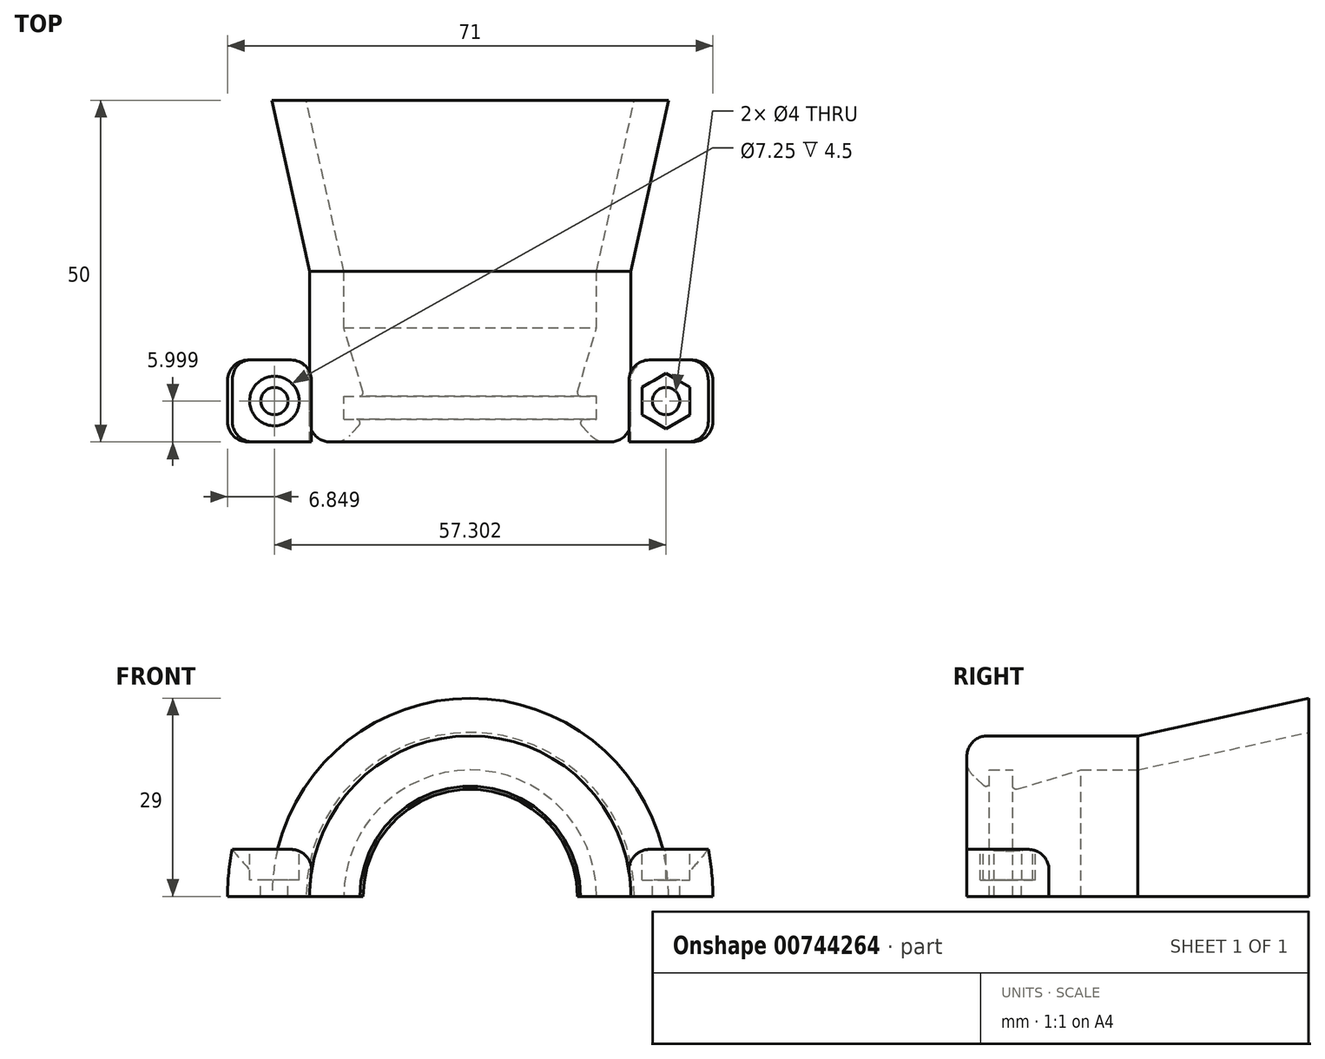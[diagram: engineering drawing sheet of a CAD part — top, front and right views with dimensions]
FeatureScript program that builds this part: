
annotation { "Feature Type Name" : "Feature", "Feature Type Description" : "" }
export const myFeature = defineFeature(function(context is Context, id is Id, definition is map)
    precondition{}
    {
        {
            var Q0;
            Q0=qCreatedBy(makeId("Top.planeOp"),FACE);
            var sketch = newSketch(context, id + "F0", { "sketchPlane" : qUnion([Q0])});
            skLineSegment(sketch, "E0", {"start": v(0, 30.3) * mm, "end": v(0, -19.7) * mm, "construction": true});
            skLineSegment(sketch, "E1", {"start": v(0, 30.3) * mm, "end": v(0, -14.7) * mm, "construction": true});
            skLineSegment(sketch, "E2", {"start": v(0, -19.7) * mm, "end": v(18.5, -19.7) * mm, "construction": true});
            skLineSegment(sketch, "E3.bottom", {"start": v(18.5, -19.7) * mm, "end": v(23.5, -19.7) * mm});
            skLineSegment(sketch, "E3.left", {"start": v(18.5, -16.4) * mm, "end": v(18.5, -13) * mm});
            skLineSegment(sketch, "E3.right", {"start": v(23.5, -19.7) * mm, "end": v(23.5, 5.3) * mm});
            skLineSegment(sketch, "E4", {"start": v(0, -14.7) * mm, "end": v(23.5, -14.7) * mm, "construction": true});
            skLineSegment(sketch, "E5", {"start": v(18.5, -14.7) * mm, "end": v(18.5, -14.7) * mm});
            skLineSegment(sketch, "E6", {"start": v(18.5, -14.7) * mm, "end": v(15.5, -14.7) * mm, "construction": true});
            skLineSegment(sketch, "E7", {"start": v(18.5, -14.7) * mm, "end": v(18.5, -16.4) * mm, "construction": true});
            skLineSegment(sketch, "E8", {"start": v(18.5, -14.7) * mm, "end": v(18.5, -13) * mm, "construction": true});
            skLineSegment(sketch, "E9", {"start": v(18.5, -16.4) * mm, "end": v(15.5, -16.4) * mm});
            skLineSegment(sketch, "E10", {"start": v(15.5, -16.4) * mm, "end": v(18.5, -19.7) * mm});
            skLineSegment(sketch, "E11", {"start": v(18.5, -13) * mm, "end": v(15.5, -13) * mm});
            skLineSegment(sketch, "E12", {"start": v(15.5, -13) * mm, "end": v(18.5, -3) * mm});
            skLineSegment(sketch, "E13.trimOffspring", {"start": v(18.5, -3) * mm, "end": v(18.5, 5.3) * mm});
            skLineSegment(sketch, "E14.bottom", {"start": v(23.5, -19.7) * mm, "end": v(30.5, -19.7) * mm});
            skLineSegment(sketch, "E14.top", {"start": v(23.5, -12.7) * mm, "end": v(30.5, -12.7) * mm});
            skLineSegment(sketch, "E14.left", {"start": v(23.5, -19.7) * mm, "end": v(23.5, -12.7) * mm});
            skLineSegment(sketch, "E14.right", {"start": v(30.5, -19.7) * mm, "end": v(30.5, -12.7) * mm});
            skLineSegment(sketch, "E15", {"start": v(0, 30.3) * mm, "end": v(18.5, 30.3) * mm, "construction": true});
            skLineSegment(sketch, "E16", {"start": v(18.5, 5.3) * mm, "end": v(24, 30.3) * mm});
            skLineSegment(sketch, "E17", {"start": v(23.5, 5.3) * mm, "end": v(29, 30.3) * mm});
            skLineSegment(sketch, "E18", {"start": v(24, 30.3) * mm, "end": v(29, 30.3) * mm});
            skPoint(sketch, "E3.top.end.orphan", {"position": v(23.5, 30.3) * mm});
            skLineSegment(sketch, "E19.bottom", {"start": v(23.5, -19.7) * mm, "end": v(35.5, -19.7) * mm});
            skLineSegment(sketch, "E19.top", {"start": v(23.5, -7.7) * mm, "end": v(35.5, -7.7) * mm});
            skLineSegment(sketch, "E19.left", {"start": v(23.5, -19.7) * mm, "end": v(23.5, -7.7) * mm});
            skLineSegment(sketch, "E19.right", {"start": v(35.5, -19.7) * mm, "end": v(35.5, -7.7) * mm});
            skSolve(sketch);
        }
        {
            var Q0;
            {var subQ3=sQuery(id+"F0.wireOp",EDGE,"E3.bottom");Q0=makeQuery(id+"F0.imprint","IMPRINT",FACE,{"disambiguationData":[TD([[makeQuery(id+"F0.imprint","IMPRINT",EDGE,{"derivedFrom":subQ3}),1.0]])]});}
            var Q1;
            Q1=sQuery(id+"F0.wireOp",EDGE,"E0");
            revolve(context, id + "F1", {"surfaceOperationType" : NewSurfaceOperationType.NEW, "entities" : qUnion([Q0]), "axis" : qUnion([Q1]), "revolveType" : RevolveType.ONE_DIRECTION, "angle" : 180 * degree});
        }
        {
            var Q0;
            Q0=makeQuery(id+"F1.opRevolve","SWEPT_EDGE",EDGE,{"disambiguationData":[OSD([sQuery(id+"F0.wireOp",EDGE,"E9"),sQuery(id+"F0.wireOp",EDGE,"E10")])]});
            var Q1;
            Q1=makeQuery(id+"F1.opRevolve","SWEPT_EDGE",EDGE,{"disambiguationData":[OSD([sQuery(id+"F0.wireOp",EDGE,"E11"),sQuery(id+"F0.wireOp",EDGE,"E12")])]});
            fillet(context, id + "F2", {"entities" : qUnion([Q0, Q1]), "radius" : 0.5 * mm, "tangentPropagation" : true, "allowEdgeOverflow" : false});
        }
        {
            var Q0;
            {var subQ0=sQuery(id+"F0.wireOp",EDGE,"E14.top");Q0=makeQuery(id+"F0.imprint","IMPRINT",FACE,{"disambiguationData":[TD([[makeQuery(id+"F0.imprint","IMPRINT",EDGE,{"derivedFrom":subQ0}),1.0]])]});}
            var Q1;
            {var subQ0=sQuery(id+"F0.wireOp",EDGE,"E14.bottom");Q1=makeQuery(id+"F0.imprint","IMPRINT",FACE,{"disambiguationData":[TD([[makeQuery(id+"F0.imprint","IMPRINT",EDGE,{"derivedFrom":subQ0}),1.0]])]});}
            var Q2;
            Q2=sQuery(id+"F0.wireOp",EDGE,"E0");
            revolve(context, id + "F3", {"surfaceOperationType" : NewSurfaceOperationType.NEW, "entities" : qUnion([Q0, Q1]), "axis" : qUnion([Q2]), "revolveType" : RevolveType.ONE_DIRECTION, "angle" : 17 * degree});
        }
        {
            var Q0;
            Q0=makeQuery(id+"F3.opRevolve","SWEPT_BODY",BODY,{"disambiguationData":[OSD([sQuery(id+"F0.wireOp",EDGE,"E3.right"),sQuery(id+"F0.wireOp",EDGE,"E14.bottom"),sQuery(id+"F0.wireOp",EDGE,"E19.bottom"),sQuery(id+"F0.wireOp",EDGE,"E19.top"),sQuery(id+"F0.wireOp",EDGE,"E19.right")])]});
            var Q1;
            Q1=sQuery(id+"F0.wireOp",EDGE,"E0");
            circularPattern(context, id + "F4", {"entities" : qUnion([Q0]), "axis" : qUnion([Q1]), "angle" : 163 * degree, "instanceCount" : 2, "equalSpace" : true});
        }
        {
            var Q0;
            Q0=makeQuery(id+"F3.opRevolve","SWEPT_FACE",FACE,{"disambiguationData":[OSD([sQuery(id+"F0.wireOp",EDGE,"E14.bottom"),sQuery(id+"F0.wireOp",EDGE,"E19.bottom")])]});
            var sketch = newSketch(context, id + "F5", { "sketchPlane" : qUnion([Q0])});
            skLineSegment(sketch, "E20.bottom", {"start": v(22.47, 6.87) * mm, "end": v(38.75, 6.87) * mm});
            skLineSegment(sketch, "E20.top", {"start": v(22.47, 10.38) * mm, "end": v(38.75, 10.38) * mm});
            skLineSegment(sketch, "E20.left", {"start": v(22.47, 6.87) * mm, "end": v(22.47, 10.38) * mm});
            skLineSegment(sketch, "E20.right", {"start": v(38.75, 6.87) * mm, "end": v(38.75, 10.38) * mm});
            skSolve(sketch);
        }
        {
            var Q0;
            {var subQ1=sQuery(id+"F0.wireOp",EDGE,"E19.bottom");var subQ2=sQuery(id+"F0.wireOp",EDGE,"E14.bottom");var subQ3=makeQuery(id+"F3.opRevolve","CAP_EDGE",EDGE,{"disambiguationData":[OSD([subQ2,subQ1])],"isStart":false});Q0=makeQuery(id+"F5.imprint","IMPRINT",FACE,{"disambiguationData":[TD([[makeQuery(id+"F5.imprint","IMPRINT",EDGE,{"derivedFrom":subQ3}),-1.0]])]});}
            extrude(context, id + "F6", {"entities" : qUnion([Q0]), "operationType" : NewBodyOperationType.REMOVE, "oppositeDirection" : true, "depth" : 15 * mm, "offsetDistance" : 25 * mm});
        }
        {
            var Q0;
            Q0=makeQuery(id+"F4.opPattern","COPY",FACE,{"derivedFrom":makeQuery(id+"F3.opRevolve","SWEPT_FACE",FACE,{"disambiguationData":[OSD([sQuery(id+"F0.wireOp",EDGE,"E14.bottom"),sQuery(id+"F0.wireOp",EDGE,"E19.bottom")])]}),"instanceName":"1"});
            var sketch = newSketch(context, id + "F7", { "sketchPlane" : qUnion([Q0])});
            skLineSegment(sketch, "E21.bottom", {"start": v(-22.47, 6.87) * mm, "end": v(-37.57, 6.87) * mm});
            skLineSegment(sketch, "E21.top", {"start": v(-22.47, 11.11) * mm, "end": v(-37.57, 11.11) * mm});
            skLineSegment(sketch, "E21.left", {"start": v(-22.47, 6.87) * mm, "end": v(-22.47, 11.11) * mm});
            skLineSegment(sketch, "E21.right", {"start": v(-37.57, 6.87) * mm, "end": v(-37.57, 11.11) * mm});
            skSolve(sketch);
        }
        {
            var Q0;
            {var subQ1=sQuery(id+"F0.wireOp",EDGE,"E19.bottom");var subQ2=sQuery(id+"F0.wireOp",EDGE,"E14.bottom");var subQ3=makeQuery(id+"F4.opPattern","COPY",EDGE,{"derivedFrom":makeQuery(id+"F3.opRevolve","CAP_EDGE",EDGE,{"disambiguationData":[OSD([subQ2,subQ1])],"isStart":true}),"instanceName":"1"});Q0=makeQuery(id+"F7.imprint","IMPRINT",FACE,{"disambiguationData":[TD([[makeQuery(id+"F7.imprint","IMPRINT",EDGE,{"derivedFrom":subQ3}),1.0]])]});}
            extrude(context, id + "F8", {"entities" : qUnion([Q0]), "operationType" : NewBodyOperationType.REMOVE, "oppositeDirection" : true, "depth" : 15 * mm, "offsetDistance" : 25 * mm});
        }
        {
            var Q0;
            Q0=makeQuery(id+"F6.boolean.opBoolean","COPY",FACE,{"derivedFrom":makeQuery(id+"F6.opExtrude","SWEPT_FACE",FACE,{"disambiguationData":[OSD([sQuery(id+"F5.wireOp",EDGE,"E20.bottom")])]})});
            var sketch = newSketch(context, id + "F9", { "sketchPlane" : qUnion([Q0])});
            skPoint(sketch, "E22", {"position": v(28.65, -13.7) * mm});
            skPoint(sketch, "E22.positionSnap0", {"position": v(22.47, -13.7) * mm});
            skPoint(sketch, "E22.positionSnap1", {"position": v(28.65, -7.7) * mm});
            skCircle(sketch, "E23.cCircle", {"center": v(28.65, -13.7) * mm, "radius": 3.5 * mm, "construction": true});
            skLineSegment(sketch, "E23.0", {"start": v(32.15, -11.68) * mm, "end": v(32.15, -15.72) * mm});
            skLineSegment(sketch, "E23.1", {"start": v(32.15, -15.72) * mm, "end": v(28.65, -17.74) * mm});
            skLineSegment(sketch, "E23.2", {"start": v(28.65, -17.74) * mm, "end": v(25.15, -15.72) * mm});
            skLineSegment(sketch, "E23.3", {"start": v(25.15, -15.72) * mm, "end": v(25.15, -11.68) * mm});
            skLineSegment(sketch, "E23.4", {"start": v(25.15, -11.68) * mm, "end": v(28.65, -9.66) * mm});
            skLineSegment(sketch, "E23.5", {"start": v(28.65, -9.66) * mm, "end": v(32.15, -11.68) * mm});
            skPoint(sketch, "E23.0.midPoint", {"position": v(32.15, -13.7) * mm});
            skCircle(sketch, "E24", {"center": v(28.65, -13.7) * mm, "radius": 2 * mm});
            skSolve(sketch);
        }
        {
            var Q0;
            Q0=makeQuery(id+"F9.imprint","IMPRINT",FACE,{"disambiguationData":[TD([[makeQuery(id+"F9.imprint","IMPRINT",EDGE,{"derivedFrom":sQuery(id+"F9.wireOp",EDGE,"E24")}),1.0]])]});
            extrude(context, id + "F10", {"entities" : qUnion([Q0]), "operationType" : NewBodyOperationType.REMOVE, "endBound" : BoundingType.THROUGH_ALL, "oppositeDirection" : true, "depth" : 25 * mm, "offsetDistance" : 25 * mm});
        }
        {
            var Q0;
            Q0=makeQuery(id+"F9.imprint","IMPRINT",FACE,{"disambiguationData":[TD([[makeQuery(id+"F9.imprint","IMPRINT",EDGE,{"derivedFrom":sQuery(id+"F9.wireOp",EDGE,"E23.0")}),-1.0]])]});
            extrude(context, id + "F11", {"entities" : qUnion([Q0]), "operationType" : NewBodyOperationType.REMOVE, "oppositeDirection" : true, "depth" : 4.5 * mm, "offsetDistance" : 25 * mm});
        }
        {
            var Q0;
            Q0=makeQuery(id+"F8.boolean.opBoolean","COPY",FACE,{"derivedFrom":makeQuery(id+"F8.opExtrude","SWEPT_FACE",FACE,{"disambiguationData":[OSD([sQuery(id+"F7.wireOp",EDGE,"E21.bottom")])]})});
            var sketch = newSketch(context, id + "F12", { "sketchPlane" : qUnion([Q0])});
            skPoint(sketch, "E25", {"position": v(-28.65, -13.7) * mm});
            skPoint(sketch, "E25.positionSnap0", {"position": v(-22.47, -13.7) * mm});
            skPoint(sketch, "E25.positionSnap1", {"position": v(-28.65, -7.7) * mm});
            skCircle(sketch, "E26", {"center": v(-28.65, -13.7) * mm, "radius": 3.62 * mm});
            skCircle(sketch, "E27", {"center": v(-28.65, -13.7) * mm, "radius": 2 * mm});
            skSolve(sketch);
        }
        {
            var Q0;
            Q0=makeQuery(id+"F12.imprint","IMPRINT",FACE,{"disambiguationData":[TD([[makeQuery(id+"F12.imprint","IMPRINT",EDGE,{"derivedFrom":sQuery(id+"F12.wireOp",EDGE,"E27")}),1.0]])]});
            extrude(context, id + "F13", {"entities" : qUnion([Q0]), "operationType" : NewBodyOperationType.REMOVE, "endBound" : BoundingType.THROUGH_ALL, "oppositeDirection" : true, "depth" : 25 * mm, "offsetDistance" : 25 * mm});
        }
        {
            var Q0;
            Q0=makeQuery(id+"F12.imprint","IMPRINT",FACE,{"disambiguationData":[TD([[makeQuery(id+"F12.imprint","IMPRINT",EDGE,{"derivedFrom":sQuery(id+"F12.wireOp",EDGE,"E26")}),1.0]])]});
            extrude(context, id + "F14", {"entities" : qUnion([Q0]), "operationType" : NewBodyOperationType.REMOVE, "oppositeDirection" : true, "depth" : 4.5 * mm, "offsetDistance" : 25 * mm});
        }
        {
            var Q0;
            Q0=makeQuery(id+"F1.opRevolve","SWEPT_EDGE",EDGE,{"disambiguationData":[OSD([sQuery(id+"F0.wireOp",EDGE,"E3.bottom"),sQuery(id+"F0.wireOp",EDGE,"E3.right"),sQuery(id+"F0.wireOp",EDGE,"E14.bottom")])]});
            var Q1;
            Q1=makeQuery(id+"F6.boolean.opBoolean","COPY",EDGE,{"derivedFrom":makeQuery(id+"F6.opExtrude","CAP_EDGE",EDGE,{"disambiguationData":[OSD([sQuery(id+"F5.wireOp",EDGE,"E20.bottom")])],"isStart":true})});
            var Q2;
            Q2=makeQuery(id+"F3.opRevolve","SWEPT_EDGE",EDGE,{"disambiguationData":[OSD([sQuery(id+"F0.wireOp",EDGE,"E19.bottom"),sQuery(id+"F0.wireOp",EDGE,"E19.right")])]});
            var Q3;
            Q3=makeQuery(id+"F3.opRevolve","SWEPT_EDGE",EDGE,{"disambiguationData":[OSD([sQuery(id+"F0.wireOp",EDGE,"E19.top"),sQuery(id+"F0.wireOp",EDGE,"E19.right")])]});
            var Q4;
            Q4=makeQuery(id+"F3.opRevolve","SWEPT_EDGE",EDGE,{"disambiguationData":[OSD([sQuery(id+"F0.wireOp",EDGE,"E3.right"),sQuery(id+"F0.wireOp",EDGE,"E19.top")])]});
            var Q5;
            Q5=makeQuery(id+"F6.boolean.opBoolean","INTERSECT",EDGE,{"derivedFrom":[makeQuery(id+"F3.opRevolve","SWEPT_FACE",FACE,{"disambiguationData":[OSD([sQuery(id+"F0.wireOp",EDGE,"E19.top")])]}),makeQuery(id+"F6.opExtrude","SWEPT_FACE",FACE,{"disambiguationData":[OSD([sQuery(id+"F5.wireOp",EDGE,"E20.bottom")])]})]});
            var Q6;
            {var subQ0=sQuery(id+"F0.wireOp",EDGE,"E3.right");Q6=makeQuery(id+"F6.boolean.opBoolean","MERGE",EDGE,{"derivedFrom":[makeQuery(id+"F3.opRevolve","CAP_EDGE",EDGE,{"disambiguationData":[OSD([subQ0])],"isStart":false})],"fromTools":[makeQuery(id+"F6.opExtrude","SWEPT_EDGE",EDGE,{"disambiguationData":[OSD([sQuery(id+"F0.wireOp",EDGE,"E3.bottom"),subQ0,sQuery(id+"F0.wireOp",EDGE,"E14.bottom"),sQuery(id+"F0.wireOp",EDGE,"E19.bottom"),sQuery(id+"F5.wireOp",EDGE,"E20.bottom"),sQuery(id+"F5.wireOp",EDGE,"E20.left")])]})]});}
            var Q7;
            Q7=makeQuery(id+"F6.boolean.opBoolean","COPY",EDGE,{"derivedFrom":makeQuery(id+"F6.opExtrude","SWEPT_EDGE",EDGE,{"disambiguationData":[OSD([sQuery(id+"F0.wireOp",EDGE,"E19.bottom"),sQuery(id+"F0.wireOp",EDGE,"E19.right"),sQuery(id+"F5.wireOp",EDGE,"E20.bottom")])]})});
            var Q8;
            {var subQ0=sQuery(id+"F0.wireOp",EDGE,"E3.right");Q8=makeQuery(id+"F8.boolean.opBoolean","MERGE",EDGE,{"derivedFrom":[makeQuery(id+"F4.opPattern","COPY",EDGE,{"derivedFrom":makeQuery(id+"F3.opRevolve","CAP_EDGE",EDGE,{"disambiguationData":[OSD([subQ0])],"isStart":true}),"instanceName":"1"})],"fromTools":[makeQuery(id+"F8.opExtrude","SWEPT_EDGE",EDGE,{"disambiguationData":[OSD([sQuery(id+"F0.wireOp",EDGE,"E3.bottom"),subQ0,sQuery(id+"F0.wireOp",EDGE,"E14.bottom"),sQuery(id+"F0.wireOp",EDGE,"E19.bottom"),sQuery(id+"F7.wireOp",EDGE,"E21.bottom"),sQuery(id+"F7.wireOp",EDGE,"E21.left")])]})]});}
            var Q9;
            Q9=makeQuery(id+"F8.boolean.opBoolean","COPY",EDGE,{"derivedFrom":makeQuery(id+"F8.opExtrude","CAP_EDGE",EDGE,{"disambiguationData":[OSD([sQuery(id+"F7.wireOp",EDGE,"E21.bottom")])],"isStart":true})});
            var Q10;
            Q10=makeQuery(id+"F8.boolean.opBoolean","INTERSECT",EDGE,{"derivedFrom":[makeQuery(id+"F4.opPattern","COPY",FACE,{"derivedFrom":makeQuery(id+"F3.opRevolve","SWEPT_FACE",FACE,{"disambiguationData":[OSD([sQuery(id+"F0.wireOp",EDGE,"E19.top")])]}),"instanceName":"1"}),makeQuery(id+"F8.opExtrude","SWEPT_FACE",FACE,{"disambiguationData":[OSD([sQuery(id+"F7.wireOp",EDGE,"E21.bottom")])]})]});
            var Q11;
            Q11=makeQuery(id+"F4.opPattern","COPY",EDGE,{"derivedFrom":makeQuery(id+"F3.opRevolve","SWEPT_EDGE",EDGE,{"disambiguationData":[OSD([sQuery(id+"F0.wireOp",EDGE,"E19.bottom"),sQuery(id+"F0.wireOp",EDGE,"E19.right")])]}),"instanceName":"1"});
            var Q12;
            Q12=makeQuery(id+"F8.boolean.opBoolean","COPY",EDGE,{"derivedFrom":makeQuery(id+"F8.opExtrude","SWEPT_EDGE",EDGE,{"disambiguationData":[OSD([sQuery(id+"F0.wireOp",EDGE,"E19.bottom"),sQuery(id+"F0.wireOp",EDGE,"E19.right"),sQuery(id+"F7.wireOp",EDGE,"E21.bottom")])]})});
            var Q13;
            Q13=makeQuery(id+"F4.opPattern","COPY",EDGE,{"derivedFrom":makeQuery(id+"F3.opRevolve","SWEPT_EDGE",EDGE,{"disambiguationData":[OSD([sQuery(id+"F0.wireOp",EDGE,"E19.top"),sQuery(id+"F0.wireOp",EDGE,"E19.right")])]}),"instanceName":"1"});
            var Q14;
            Q14=makeQuery(id+"F4.opPattern","COPY",EDGE,{"derivedFrom":makeQuery(id+"F3.opRevolve","SWEPT_EDGE",EDGE,{"disambiguationData":[OSD([sQuery(id+"F0.wireOp",EDGE,"E3.right"),sQuery(id+"F0.wireOp",EDGE,"E19.top")])]}),"instanceName":"1"});
            var Q15;
            Q15=makeQuery(id+"F1.opRevolve","SWEPT_EDGE",EDGE,{"disambiguationData":[OSD([sQuery(id+"F0.wireOp",EDGE,"E3.bottom"),sQuery(id+"F0.wireOp",EDGE,"E10")])]});
            fillet(context, id + "F15", {"entities" : qUnion([Q0, Q1, Q2, Q3, Q4, Q5, Q6, Q7, Q8, Q9, Q10, Q11, Q12, Q13, Q14, Q15]), "radius" : 3 * mm, "tangentPropagation" : true, "allowEdgeOverflow" : false});
        }
    });
